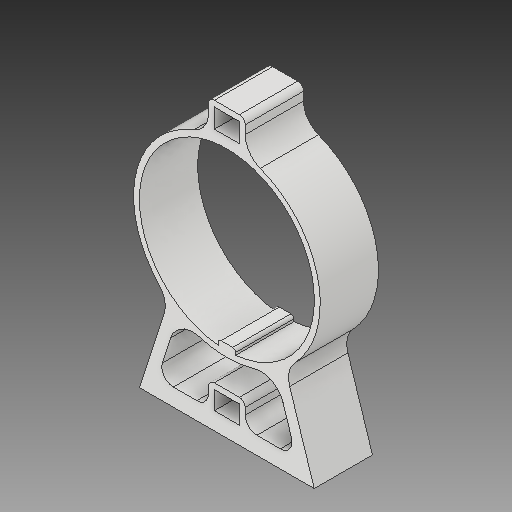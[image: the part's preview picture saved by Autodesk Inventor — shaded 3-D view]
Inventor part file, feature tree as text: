
AUTODESK INVENTOR PART (.ipt)
format: ipt  version: 2018 (Build 220112000, 112)  size: 214,016 bytes
history: native  units: mm
features: extrude x1, fillet x1, sketch x1
ambient origin geometry x8: Origin, YZ Plane, XZ Plane, XY Plane, X Axis, Y Axis, Z Axis, Center Point
bodies: Solid1 (feature_tree)
feature tree (3):
  extrude  "Extrusion1"  Depth=1.0mm
  fillet  "Fillet1"  Radius=30.0mm
  sketch  "Sketch1"  dims[d0=28.0mm d1=1.0mm d2=30.0mm d3=30.03mm d4=20.0mm d5=3.0mm d6=2.0mm d8=10.0mm d9=0.0mm d10=3.0mm d12=1.0mm d13=0.5mm d14=3.0mm d15=4.0mm d16=0.15mm d17=1.0mm d18=4.0mm d19=2.0mm d20=1.0mm d21=4.0mm d22=3.0mm d23=17.0mm d24=0.15mm d25=1.0mm d26=1.0mm d27=1.0mm]
